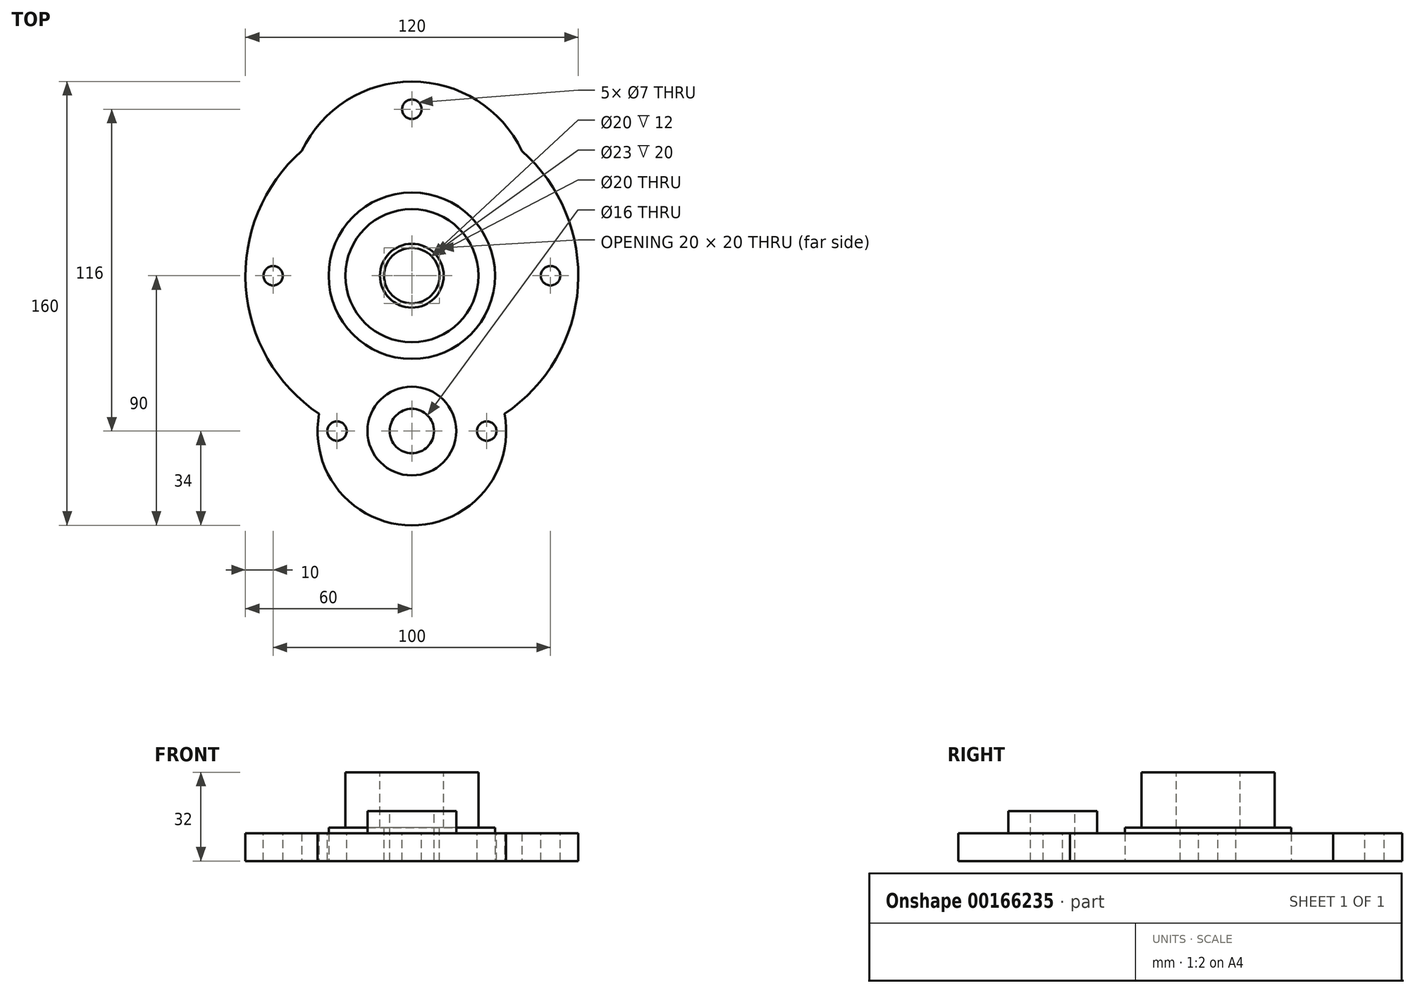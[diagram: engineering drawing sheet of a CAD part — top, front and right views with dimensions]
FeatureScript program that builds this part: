
annotation { "Feature Type Name" : "Feature", "Feature Type Description" : "" }
export const myFeature = defineFeature(function(context is Context, id is Id, definition is map)
    precondition{}
    {
        {
            var Q0;
            Q0=qCreatedBy(makeId("Top.planeOp"),FACE);
            var sketch = newSketch(context, id + "F16", { "sketchPlane" : qUnion([Q0])});
            skCircle(sketch, "E0", {"center": v(0, 0) * mm, "radius": 1524 * mm});
            skArc(sketch, "E1", {"start": v(-39.69, 45) * mm, "mid": v(-59.87, -3.95) * mm, "end": v(-33.43, -49.82) * mm});
            skCircle(sketch, "E2", {"center": v(188.3, 591.98) * mm, "radius": 241.72 * mm});
            skCircle(sketch, "E3", {"center": v(3.37, 59.9) * mm, "radius": 1117.6 * mm});
            skCircle(sketch, "E4", {"center": v(0, 49.62) * mm, "radius": 1117.6 * mm});
            skArc(sketch, "E5", {"start": v(39.69, 45) * mm, "mid": v(0, 70) * mm, "end": v(-39.69, 45) * mm});
            skArc(sketch, "E6", {"start": v(-33.43, -49.82) * mm, "mid": v(0, -90) * mm, "end": v(33.43, -49.82) * mm});
            skArc(sketch, "E7.trimOffspring", {"start": v(33.43, -49.82) * mm, "mid": v(59.87, -3.95) * mm, "end": v(39.69, 45) * mm});
            skSolve(sketch);
        }
        {
            var Q0;
            Q0=makeQuery(id+"F16.imprint","IMPRINT",FACE,{"disambiguationData":[TD([[makeQuery(id+"F16.imprint","IMPRINT",EDGE,{"derivedFrom":sQuery(id+"F16.wireOp",EDGE,"E1")}),1.0]])]});
            extrude(context, id + "F0", {"entities" : qUnion([Q0]), "depth" : 10 * mm});
        }
        {
            var Q0;
            Q0=qCreatedBy(makeId("Top.planeOp"),FACE);
            var sketch = newSketch(context, id + "F17", { "sketchPlane" : qUnion([Q0])});
            skCircle(sketch, "E8", {"center": v(0, 0) * mm, "radius": 30 * mm});
            skSolve(sketch);
        }
        {
            var Q0;
            Q0 = qSketchRegion(id + "F17", true);
            extrude(context, id + "F18", {"entities" : qUnion([Q0]), "depth" : 12 * mm});
        }
        {
            var Q0;
            Q0=makeQuery(id+"F18.opExtrude","CAP_FACE",FACE,{"disambiguationData":[OSD([sQuery(id+"F17.wireOp",EDGE,"E8")])],"isStart":false});
            var sketch = newSketch(context, id + "F1", { "sketchPlane" : qUnion([Q0])});
            skCircle(sketch, "E9", {"center": v(0, 0) * mm, "radius": 24 * mm});
            skSolve(sketch);
        }
        {
            var Q0;
            Q0=makeQuery(id+"F1.imprint","IMPRINT",FACE,{"disambiguationData":[TD([[makeQuery(id+"F1.imprint","IMPRINT",EDGE,{"derivedFrom":sQuery(id+"F1.wireOp",EDGE,"E9")}),1.0]])]});
            extrude(context, id + "F2", {"entities" : qUnion([Q0]), "operationType" : NewBodyOperationType.ADD, "depth" : 20 * mm});
        }
        {
            var Q0;
            Q0=makeQuery(id+"F2.opExtrude","CAP_FACE",FACE,{"disambiguationData":[OSD([sQuery(id+"F1.wireOp",EDGE,"E9")])],"isStart":false});
            var sketch = newSketch(context, id + "F3", { "sketchPlane" : qUnion([Q0])});
            skCircle(sketch, "E10", {"center": v(0, 0) * mm, "radius": 10 * mm});
            skSolve(sketch);
        }
        {
            var Q0;
            Q0=makeQuery(id+"F3.imprint","IMPRINT",FACE,{"disambiguationData":[TD([[makeQuery(id+"F3.imprint","IMPRINT",EDGE,{"derivedFrom":sQuery(id+"F3.wireOp",EDGE,"E10")}),1.0]])]});
            extrude(context, id + "F4", {"entities" : qUnion([Q0]), "operationType" : NewBodyOperationType.REMOVE, "oppositeDirection" : true, "depth" : 25 * mm});
        }
        {
            var Q0;
            Q0=makeQuery(id+"F18.opExtrude","CAP_FACE",FACE,{"disambiguationData":[OSD([sQuery(id+"F17.wireOp",EDGE,"E8")])],"isStart":true});
            var sketch = newSketch(context, id + "F19", { "sketchPlane" : qUnion([Q0])});
            skCircle(sketch, "E11", {"center": v(0, 0) * mm, "radius": 10 * mm});
            skSolve(sketch);
        }
        {
            var Q0;
            Q0=makeQuery(id+"F19.imprint","IMPRINT",FACE,{"disambiguationData":[TD([[makeQuery(id+"F19.imprint","IMPRINT",EDGE,{"derivedFrom":sQuery(id+"F19.wireOp",EDGE,"E11")}),1.0]])]});
            extrude(context, id + "F5", {"entities" : qUnion([Q0]), "operationType" : NewBodyOperationType.REMOVE, "oppositeDirection" : true, "depth" : 30 * mm});
        }
        {
            var Q0;
            Q0=makeQuery(id+"F2.opExtrude","CAP_FACE",FACE,{"disambiguationData":[OSD([sQuery(id+"F1.wireOp",EDGE,"E9")])],"isStart":false});
            var sketch = newSketch(context, id + "F6", { "sketchPlane" : qUnion([Q0])});
            skCircle(sketch, "E12", {"center": v(0, 0) * mm, "radius": 10 * mm});
            skSolve(sketch);
        }
        {
            var Q0;
            Q0=makeQuery(id+"F6.imprint","IMPRINT",FACE,{"disambiguationData":[TD([[makeQuery(id+"F6.imprint","IMPRINT",EDGE,{"derivedFrom":sQuery(id+"F6.wireOp",EDGE,"E12")}),1.0]])]});
            extrude(context, id + "F7", {"entities" : qUnion([Q0]), "operationType" : NewBodyOperationType.REMOVE, "oppositeDirection" : true, "depth" : 30 * mm});
        }
        {
            var Q0;
            Q0=makeQuery(id+"F0.opExtrude","CAP_FACE",FACE,{"disambiguationData":[OSD([sQuery(id+"F16.wireOp",EDGE,"E1"),sQuery(id+"F16.wireOp",EDGE,"E5"),sQuery(id+"F16.wireOp",EDGE,"E6"),sQuery(id+"F16.wireOp",EDGE,"E7.trimOffspring")])],"isStart":false});
            var sketch = newSketch(context, id + "F20", { "sketchPlane" : qUnion([Q0])});
            skCircle(sketch, "E13", {"center": v(0, -56) * mm, "radius": 16 * mm});
            skSolve(sketch);
        }
        {
            var Q0;
            Q0=makeQuery(id+"F20.imprint","IMPRINT",FACE,{"disambiguationData":[TD([[makeQuery(id+"F20.imprint","IMPRINT",EDGE,{"derivedFrom":sQuery(id+"F20.wireOp",EDGE,"E13")}),1.0]])]});
            extrude(context, id + "F8", {"entities" : qUnion([Q0]), "operationType" : NewBodyOperationType.ADD, "depth" : 8 * mm});
        }
        {
            var Q0;
            Q0=makeQuery(id+"F8.opExtrude","CAP_FACE",FACE,{"disambiguationData":[OSD([sQuery(id+"F20.wireOp",EDGE,"E13")])],"isStart":false});
            var sketch = newSketch(context, id + "F21", { "sketchPlane" : qUnion([Q0])});
            skCircle(sketch, "E14", {"center": v(0, -56) * mm, "radius": 8 * mm});
            skSolve(sketch);
        }
        {
            var Q0;
            Q0=makeQuery(id+"F21.imprint","IMPRINT",FACE,{"disambiguationData":[TD([[makeQuery(id+"F21.imprint","IMPRINT",EDGE,{"derivedFrom":sQuery(id+"F21.wireOp",EDGE,"E14")}),1.0]])]});
            extrude(context, id + "F9", {"entities" : qUnion([Q0]), "operationType" : NewBodyOperationType.REMOVE, "oppositeDirection" : true, "depth" : 25 * mm});
        }
        {
            var Q0;
            Q0=makeQuery(id+"F2.opExtrude","CAP_FACE",FACE,{"disambiguationData":[OSD([sQuery(id+"F1.wireOp",EDGE,"E9")])],"isStart":false});
            var sketch = newSketch(context, id + "F10", { "sketchPlane" : qUnion([Q0])});
            skCircle(sketch, "E15", {"center": v(0, 0) * mm, "radius": 10 * mm});
            skSolve(sketch);
        }
        {
            var Q0;
            Q0=makeQuery(id+"F10.imprint","IMPRINT",FACE,{"disambiguationData":[TD([[makeQuery(id+"F10.imprint","IMPRINT",EDGE,{"derivedFrom":sQuery(id+"F10.wireOp",EDGE,"E15")}),1.0]])]});
            extrude(context, id + "F11", {"entities" : qUnion([Q0]), "operationType" : NewBodyOperationType.REMOVE, "oppositeDirection" : true, "depth" : 35 * mm});
        }
        {
            var Q0;
            Q0=makeQuery(id+"F2.opExtrude","CAP_FACE",FACE,{"disambiguationData":[OSD([sQuery(id+"F1.wireOp",EDGE,"E9")])],"isStart":false});
            var sketch = newSketch(context, id + "F12", { "sketchPlane" : qUnion([Q0])});
            skCircle(sketch, "E16", {"center": v(0, 0) * mm, "radius": 11.5 * mm});
            skSolve(sketch);
        }
        {
            var Q0;
            Q0=makeQuery(id+"F12.imprint","IMPRINT",FACE,{"disambiguationData":[TD([[makeQuery(id+"F12.imprint","IMPRINT",EDGE,{"derivedFrom":sQuery(id+"F12.wireOp",EDGE,"E16")}),1.0]])]});
            extrude(context, id + "F13", {"entities" : qUnion([Q0]), "operationType" : NewBodyOperationType.REMOVE, "oppositeDirection" : true, "depth" : 20 * mm});
        }
        {
            var Q0;
            Q0=makeQuery(id+"F0.opExtrude","CAP_FACE",FACE,{"disambiguationData":[OSD([sQuery(id+"F16.wireOp",EDGE,"E1"),sQuery(id+"F16.wireOp",EDGE,"E5"),sQuery(id+"F16.wireOp",EDGE,"E6"),sQuery(id+"F16.wireOp",EDGE,"E7.trimOffspring")])],"isStart":false});
            var sketch = newSketch(context, id + "F14", { "sketchPlane" : qUnion([Q0])});
            skCircle(sketch, "E17", {"center": v(50, 0) * mm, "radius": 3.5 * mm});
            skCircle(sketch, "E18", {"center": v(-50, 0) * mm, "radius": 3.5 * mm});
            skCircle(sketch, "E19", {"center": v(0, 60) * mm, "radius": 3.5 * mm});
            skLineSegment(sketch, "E20", {"start": v(0, -56) * mm, "end": v(0, -56) * mm});
            skLineSegment(sketch, "E21", {"start": v(-27, -56) * mm, "end": v(-27, -56) * mm});
            skCircle(sketch, "E22", {"center": v(27, -56) * mm, "radius": 3.5 * mm});
            skCircle(sketch, "E23", {"center": v(-27, -56) * mm, "radius": 3.5 * mm});
            skPoint(sketch, "E24.center.orphan", {"position": v(9.86, -31.15) * mm});
            skPoint(sketch, "E25.center.orphan", {"position": v(-44.14, -26.15) * mm});
            skSolve(sketch);
        }
        {
            var Q0;
            Q0=makeQuery(id+"F14.imprint","IMPRINT",FACE,{"disambiguationData":[TD([[makeQuery(id+"F14.imprint","IMPRINT",EDGE,{"derivedFrom":sQuery(id+"F14.wireOp",EDGE,"E23")}),1.0]])]});
            var Q1;
            Q1=makeQuery(id+"F14.imprint","IMPRINT",FACE,{"disambiguationData":[TD([[makeQuery(id+"F14.imprint","IMPRINT",EDGE,{"derivedFrom":sQuery(id+"F14.wireOp",EDGE,"E22")}),1.0]])]});
            var Q2;
            Q2=makeQuery(id+"F14.imprint","IMPRINT",FACE,{"disambiguationData":[TD([[makeQuery(id+"F14.imprint","IMPRINT",EDGE,{"derivedFrom":sQuery(id+"F14.wireOp",EDGE,"E18")}),1.0]])]});
            var Q3;
            Q3=makeQuery(id+"F14.imprint","IMPRINT",FACE,{"disambiguationData":[TD([[makeQuery(id+"F14.imprint","IMPRINT",EDGE,{"derivedFrom":sQuery(id+"F14.wireOp",EDGE,"E17")}),1.0]])]});
            var Q4;
            Q4=makeQuery(id+"F14.imprint","IMPRINT",FACE,{"disambiguationData":[TD([[makeQuery(id+"F14.imprint","IMPRINT",EDGE,{"derivedFrom":sQuery(id+"F14.wireOp",EDGE,"E19")}),1.0]])]});
            extrude(context, id + "F15", {"entities" : qUnion([Q0, Q1, Q2, Q3, Q4]), "operationType" : NewBodyOperationType.REMOVE, "oppositeDirection" : true, "depth" : 10 * mm});
        }
    });
